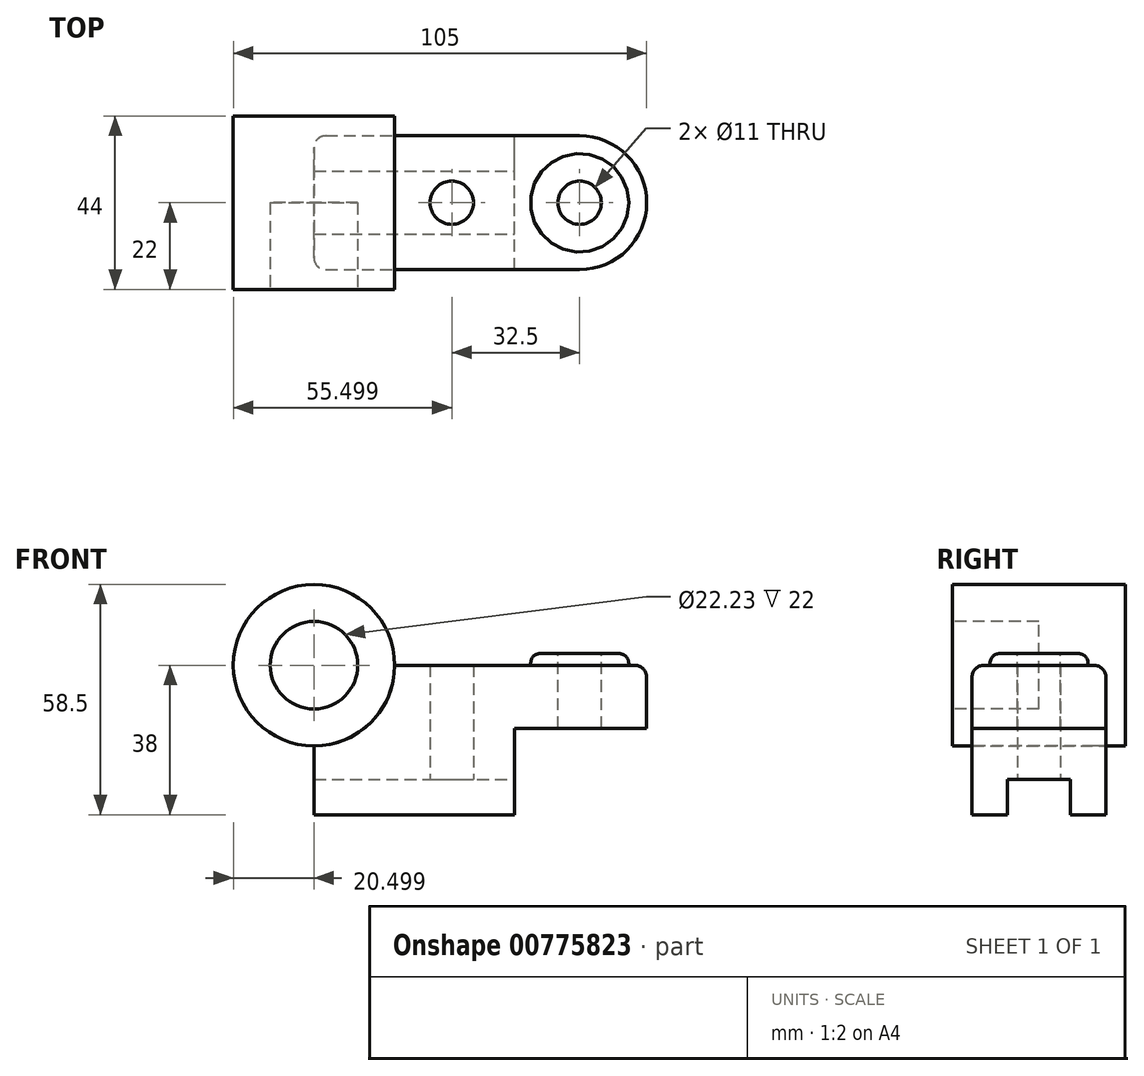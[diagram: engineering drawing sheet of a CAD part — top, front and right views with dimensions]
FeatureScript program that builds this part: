
annotation { "Feature Type Name" : "Feature", "Feature Type Description" : "" }
export const myFeature = defineFeature(function(context is Context, id is Id, definition is map)
    precondition{}
    {
        {
            var Q0;
            Q0=qCreatedBy(makeId("Front.planeOp"),FACE);
            var sketch = newSketch(context, id + "F0", { "sketchPlane" : qUnion([Q0])});
            skLineSegment(sketch, "E0.bottom", {"start": v(-36.23, 1.48) * mm, "end": v(48.27, 1.48) * mm});
            skLineSegment(sketch, "E0.top", {"start": v(-36.23, -36.52) * mm, "end": v(48.27, -36.52) * mm});
            skLineSegment(sketch, "E0.left", {"start": v(-36.23, 1.48) * mm, "end": v(-36.23, -36.52) * mm});
            skLineSegment(sketch, "E0.right", {"start": v(48.27, 1.48) * mm, "end": v(48.27, -36.52) * mm});
            skLineSegment(sketch, "E1", {"start": v(48.27, -36.52) * mm, "end": v(14.77, -36.52) * mm});
            skLineSegment(sketch, "E2", {"start": v(14.77, -36.52) * mm, "end": v(14.77, -14.52) * mm});
            skLineSegment(sketch, "E3", {"start": v(14.77, -14.52) * mm, "end": v(48.27, -14.52) * mm});
            skLineSegment(sketch, "E4", {"start": v(48.27, -14.52) * mm, "end": v(48.27, -36.52) * mm});
            skSolve(sketch);
        }
        {
            var Q0;
            Q0=makeQuery(id+"F0.imprint","IMPRINT",FACE,{"disambiguationData":[TD([[makeQuery(id+"F0.imprint","IMPRINT",EDGE,{"derivedFrom":sQuery(id+"F0.wireOp",EDGE,"E0.bottom")}),-1.0]])]});
            extrude(context, id + "F1", {"entities" : qUnion([Q0]), "depth" : 34 * mm, "offsetDistance" : 25 * mm});
        }
        {
            var Q0;
            Q0=makeQuery(id+"F1.opExtrude","SWEPT_FACE",FACE,{"disambiguationData":[OSD([sQuery(id+"F0.wireOp",EDGE,"E2")])]});
            var sketch = newSketch(context, id + "F2", { "sketchPlane" : qUnion([Q0])});
            skLineSegment(sketch, "E5", {"start": v(-34, -36.52) * mm, "end": v(-25, -36.52) * mm});
            skLineSegment(sketch, "E6", {"start": v(-25, -36.52) * mm, "end": v(-25, -27.52) * mm});
            skLineSegment(sketch, "E7", {"start": v(-25, -27.52) * mm, "end": v(-9, -27.52) * mm});
            skLineSegment(sketch, "E8", {"start": v(-9, -27.52) * mm, "end": v(-9, -36.52) * mm});
            skLineSegment(sketch, "E9", {"start": v(-9, -36.52) * mm, "end": v(-25, -36.52) * mm});
            skSolve(sketch);
        }
        {
            var Q0;
            Q0=makeQuery(id+"F2.imprint","IMPRINT",FACE,{"disambiguationData":[TD([[makeQuery(id+"F2.imprint","IMPRINT",EDGE,{"derivedFrom":sQuery(id+"F2.wireOp",EDGE,"E6")}),-1.0]])]});
            extrude(context, id + "F3", {"entities" : qUnion([Q0]), "operationType" : NewBodyOperationType.REMOVE, "oppositeDirection" : true, "depth" : 100 * mm, "offsetDistance" : 25 * mm});
        }
        {
            var Q0;
            Q0=makeQuery(id+"F1.opExtrude","CAP_EDGE",EDGE,{"disambiguationData":[OSD([sQuery(id+"F0.wireOp",EDGE,"E0.right")])],"isStart":false});
            fillet(context, id + "F4", {"entities" : qUnion([Q0]), "radius" : 17 * mm, "tangentPropagation" : true, "allowEdgeOverflow" : false});
        }
        {
            var Q0;
            Q0=makeQuery(id+"F1.opExtrude","CAP_EDGE",EDGE,{"disambiguationData":[OSD([sQuery(id+"F0.wireOp",EDGE,"E0.right")])],"isStart":true});
            fillet(context, id + "F5", {"entities" : qUnion([Q0]), "radius" : 17 * mm, "tangentPropagation" : true, "allowEdgeOverflow" : false});
        }
        {
            var Q0;
            Q0=makeQuery(id+"F1.opExtrude","SWEPT_FACE",FACE,{"disambiguationData":[OSD([sQuery(id+"F0.wireOp",EDGE,"E0.bottom")])]});
            var sketch = newSketch(context, id + "F6", { "sketchPlane" : qUnion([Q0])});
            skLineSegment(sketch, "E10", {"start": v(31.27, 0) * mm, "end": v(31.27, -17) * mm});
            skCircle(sketch, "E11", {"center": v(31.27, -17) * mm, "radius": 12.5 * mm});
            skCircle(sketch, "E12", {"center": v(31.27, -17) * mm, "radius": 5.5 * mm});
            skSolve(sketch);
        }
        {
            var Q0;
            Q0=makeQuery(id+"F6.imprint","IMPRINT",FACE,{"disambiguationData":[TD([[makeQuery(id+"F6.imprint","IMPRINT",EDGE,{"derivedFrom":sQuery(id+"F6.wireOp",EDGE,"E12")}),1.0]])]});
            extrude(context, id + "F7", {"entities" : qUnion([Q0]), "operationType" : NewBodyOperationType.REMOVE, "oppositeDirection" : true, "depth" : 25 * mm, "offsetDistance" : 25 * mm});
        }
        {
            var Q0;
            Q0=makeQuery(id+"F1.opExtrude","SWEPT_FACE",FACE,{"disambiguationData":[OSD([sQuery(id+"F0.wireOp",EDGE,"E0.bottom")])]});
            var sketch = newSketch(context, id + "F8", { "sketchPlane" : qUnion([Q0])});
            skLineSegment(sketch, "E13", {"start": v(31.27, 0) * mm, "end": v(31.27, -17) * mm});
            skCircle(sketch, "E14", {"center": v(31.27, -17) * mm, "radius": 12.5 * mm});
            skSolve(sketch);
        }
        {
            var Q0;
            Q0=makeQuery(id+"F8.imprint","IMPRINT",FACE,{"disambiguationData":[TD([[makeQuery(id+"F8.imprint","IMPRINT",EDGE,{"derivedFrom":sQuery(id+"F8.wireOp",EDGE,"E14")}),1.0]])]});
            extrude(context, id + "F9", {"entities" : qUnion([Q0]), "operationType" : NewBodyOperationType.ADD, "depth" : 3 * mm, "offsetDistance" : 25 * mm});
        }
        {
            var Q0;
            Q0=makeQuery(id+"F1.opExtrude","CAP_FACE",FACE,{"disambiguationData":[OSD([sQuery(id+"F0.wireOp",EDGE,"E0.bottom"),sQuery(id+"F0.wireOp",EDGE,"E0.top"),sQuery(id+"F0.wireOp",EDGE,"E0.left"),sQuery(id+"F0.wireOp",EDGE,"E0.right"),sQuery(id+"F0.wireOp",EDGE,"E2"),sQuery(id+"F0.wireOp",EDGE,"E3")])],"isStart":false});
            var sketch = newSketch(context, id + "F10", { "sketchPlane" : qUnion([Q0])});
            skCircle(sketch, "E15", {"center": v(-36.23, 1.48) * mm, "radius": 20.5 * mm});
            skCircle(sketch, "E16", {"center": v(-36.23, 1.48) * mm, "radius": 11.12 * mm});
            skSolve(sketch);
        }
        {
            var Q0;
            {var subQ0=sQuery(id+"F10.wireOp",EDGE,"E16");var subQ1=makeQuery(id+"F1.opExtrude","CAP_EDGE",EDGE,{"disambiguationData":[OSD([sQuery(id+"F0.wireOp",EDGE,"E0.left")])],"isStart":false});var subQ2=makeQuery(id+"F10.imprint","INTERSECT",VERTEX,{"derivedFrom":[subQ1,subQ0]});Q0=makeQuery(id+"F10.imprint","IMPRINT",FACE,{"disambiguationData":[TD([[makeQuery(id+"F10.imprint","IMPRINT",EDGE,{"disambiguationData":[TD([[subQ2,-1.0]])],"derivedFrom":subQ0}),1.0]])]});}
            var Q1;
            {var subQ0=sQuery(id+"F10.wireOp",EDGE,"E15");var subQ1=makeQuery(id+"F1.opExtrude","CAP_EDGE",EDGE,{"disambiguationData":[OSD([sQuery(id+"F0.wireOp",EDGE,"E0.left")])],"isStart":false});var subQ2=makeQuery(id+"F10.imprint","INTERSECT",VERTEX,{"derivedFrom":[subQ1,subQ0]});Q1=makeQuery(id+"F10.imprint","IMPRINT",FACE,{"disambiguationData":[TD([[makeQuery(id+"F10.imprint","IMPRINT",EDGE,{"disambiguationData":[TD([[subQ2,-1.0]])],"derivedFrom":subQ0}),1.0]])]});}
            extrude(context, id + "F11", {"entities" : qUnion([Q0, Q1]), "operationType" : NewBodyOperationType.REMOVE, "oppositeDirection" : true, "depth" : 50 * mm, "offsetDistance" : 25 * mm});
        }
        {
            var Q0;
            Q0=qCreatedBy(makeId("Front.planeOp"),FACE);
            var sketch = newSketch(context, id + "F12", { "sketchPlane" : qUnion([Q0])});
            skCircle(sketch, "E17", {"center": v(-36.23, 1.48) * mm, "radius": 20.5 * mm});
            skCircle(sketch, "E18", {"center": v(-36.23, 1.48) * mm, "radius": 11.12 * mm});
            skSolve(sketch);
        }
        {
            var Q0;
            Q0=makeQuery(id+"F12.imprint","IMPRINT",FACE,{"disambiguationData":[TD([[makeQuery(id+"F12.imprint","IMPRINT",EDGE,{"derivedFrom":sQuery(id+"F12.wireOp",EDGE,"E18")}),1.0]])]});
            var Q1;
            Q1=makeQuery(id+"F12.imprint","IMPRINT",FACE,{"disambiguationData":[TD([[makeQuery(id+"F12.imprint","IMPRINT",EDGE,{"derivedFrom":sQuery(id+"F12.wireOp",EDGE,"E17")}),1.0]])]});
            extrude(context, id + "F13", {"entities" : qUnion([Q0, Q1]), "depth" : 5 * mm, "offsetDistance" : 25 * mm});
        }
        {
            var Q0;
            Q0=makeQuery(id+"F13.opExtrude","CAP_FACE",FACE,{"disambiguationData":[OSD([sQuery(id+"F12.wireOp",EDGE,"E17")])],"isStart":false});
            var sketch = newSketch(context, id + "F14", { "sketchPlane" : qUnion([Q0])});
            skCircle(sketch, "E19", {"center": v(-36.23, 1.48) * mm, "radius": 20.5 * mm});
            skSolve(sketch);
        }
        {
            var Q0;
            Q0 = qSketchRegion(id + "F14", true);
            extrude(context, id + "F15", {"entities" : qUnion([Q0]), "operationType" : NewBodyOperationType.ADD, "depth" : 39 * mm, "offsetDistance" : 25 * mm});
        }
        {
            var Q0;
            Q0=makeQuery(id+"F13.opExtrude","CAP_FACE",FACE,{"disambiguationData":[OSD([sQuery(id+"F12.wireOp",EDGE,"E17")])],"isStart":true});
            var sketch = newSketch(context, id + "F16", { "sketchPlane" : qUnion([Q0])});
            skCircle(sketch, "E20", {"center": v(36.23, 1.48) * mm, "radius": 20.5 * mm});
            skSolve(sketch);
        }
        {
            var Q0;
            Q0 = qSketchRegion(id + "F16", true);
            extrude(context, id + "F17", {"entities" : qUnion([Q0]), "operationType" : NewBodyOperationType.ADD, "depth" : 5 * mm, "offsetDistance" : 25 * mm});
        }
        {
            var Q0;
            Q0=makeQuery(id+"F15.opExtrude","CAP_FACE",FACE,{"disambiguationData":[OSD([sQuery(id+"F14.wireOp",EDGE,"E19")])],"isStart":false});
            var sketch = newSketch(context, id + "F18", { "sketchPlane" : qUnion([Q0])});
            skCircle(sketch, "E21", {"center": v(-36.23, 1.48) * mm, "radius": 20.5 * mm});
            skSolve(sketch);
        }
        {
            var Q0;
            Q0 = qSketchRegion(id + "F18", true);
            extrude(context, id + "F19", {"entities" : qUnion([Q0]), "operationType" : NewBodyOperationType.REMOVE, "oppositeDirection" : true, "depth" : 5 * mm, "offsetDistance" : 25 * mm});
        }
        {
            var Q0;
            Q0=makeQuery(id+"F19.boolean.opBoolean","COPY",FACE,{"derivedFrom":makeQuery(id+"F19.opExtrude","CAP_FACE",FACE,{"disambiguationData":[OSD([sQuery(id+"F18.wireOp",EDGE,"E21")])],"isStart":false})});
            var sketch = newSketch(context, id + "F20", { "sketchPlane" : qUnion([Q0])});
            skCircle(sketch, "E22", {"center": v(-36.23, 1.48) * mm, "radius": 11.12 * mm});
            skSolve(sketch);
        }
        {
            var Q0;
            Q0=makeQuery(id+"F20.imprint","IMPRINT",FACE,{"disambiguationData":[TD([[makeQuery(id+"F20.imprint","IMPRINT",EDGE,{"derivedFrom":sQuery(id+"F20.wireOp",EDGE,"E22")}),1.0]])]});
            extrude(context, id + "F21", {"entities" : qUnion([Q0]), "operationType" : NewBodyOperationType.REMOVE, "oppositeDirection" : true, "depth" : 22 * mm, "offsetDistance" : 25 * mm});
        }
        {
            var Q0;
            Q0=makeQuery(id+"F3.boolean.opBoolean","COPY",FACE,{"derivedFrom":makeQuery(id+"F3.opExtrude","SWEPT_FACE",FACE,{"disambiguationData":[OSD([sQuery(id+"F2.wireOp",EDGE,"E7")])]})});
            var sketch = newSketch(context, id + "F22", { "sketchPlane" : qUnion([Q0])});
            skLineSegment(sketch, "E23", {"start": v(-36.23, 9) * mm, "end": v(-36.23, 17) * mm});
            skLineSegment(sketch, "E24", {"start": v(-36.23, 17) * mm, "end": v(-1.23, 17) * mm});
            skCircle(sketch, "E25", {"center": v(-1.23, 17) * mm, "radius": 5.5 * mm});
            skSolve(sketch);
        }
        {
            var Q0;
            Q0=makeQuery(id+"F22.imprint","IMPRINT",FACE,{"disambiguationData":[TD([[makeQuery(id+"F22.imprint","IMPRINT",EDGE,{"derivedFrom":sQuery(id+"F22.wireOp",EDGE,"E25")}),1.0]])]});
            extrude(context, id + "F23", {"entities" : qUnion([Q0]), "operationType" : NewBodyOperationType.REMOVE, "oppositeDirection" : true, "depth" : 25 * mm, "offsetDistance" : 25 * mm});
        }
        {
            var Q0;
            Q0=makeQuery(id+"F23.boolean.opBoolean","COPY",FACE,{"derivedFrom":makeQuery(id+"F23.opExtrude","CAP_FACE",FACE,{"disambiguationData":[OSD([sQuery(id+"F22.wireOp",EDGE,"E25")])],"isStart":false})});
            extrude(context, id + "F24", {"entities" : qUnion([Q0]), "operationType" : NewBodyOperationType.REMOVE, "oppositeDirection" : true, "depth" : 25 * mm, "offsetDistance" : 25 * mm});
        }
        {
            var Q0;
            Q0=makeQuery(id+"F1.opExtrude","CAP_EDGE",EDGE,{"disambiguationData":[OSD([sQuery(id+"F0.wireOp",EDGE,"E0.bottom")])],"isStart":true});
            var Q1;
            Q1=makeQuery(id+"F5.opFillet","BLEND_EDGE",EDGE,{"blendedFrom":[makeQuery(id+"F1.opExtrude","CAP_EDGE",EDGE,{"disambiguationData":[OSD([sQuery(id+"F0.wireOp",EDGE,"E0.right")])],"isStart":true}),makeQuery(id+"F1.opExtrude","SWEPT_FACE",FACE,{"disambiguationData":[OSD([sQuery(id+"F0.wireOp",EDGE,"E0.bottom")])]})],"blendedInto":[makeQuery(id+"F1.opExtrude","SWEPT_FACE",FACE,{"disambiguationData":[OSD([sQuery(id+"F0.wireOp",EDGE,"E0.bottom")])]})]});
            var Q2;
            Q2=makeQuery(id+"F4.opFillet","BLEND_EDGE",EDGE,{"blendedFrom":[makeQuery(id+"F1.opExtrude","CAP_EDGE",EDGE,{"disambiguationData":[OSD([sQuery(id+"F0.wireOp",EDGE,"E0.right")])],"isStart":false}),makeQuery(id+"F1.opExtrude","SWEPT_FACE",FACE,{"disambiguationData":[OSD([sQuery(id+"F0.wireOp",EDGE,"E0.bottom")])]})],"blendedInto":[makeQuery(id+"F1.opExtrude","SWEPT_FACE",FACE,{"disambiguationData":[OSD([sQuery(id+"F0.wireOp",EDGE,"E0.bottom")])]})]});
            var Q3;
            Q3=makeQuery(id+"F1.opExtrude","CAP_EDGE",EDGE,{"disambiguationData":[OSD([sQuery(id+"F0.wireOp",EDGE,"E0.bottom")])],"isStart":false});
            var Q4;
            Q4=makeQuery(id+"F11.boolean.opBoolean","COPY",EDGE,{"derivedFrom":makeQuery(id+"F11.opExtrude","SWEPT_EDGE",EDGE,{"disambiguationData":[OSD([sQuery(id+"F0.wireOp",EDGE,"E0.bottom"),sQuery(id+"F10.wireOp",EDGE,"E15")])]})});
            fillet(context, id + "F25", {"entities" : qUnion([Q0, Q1, Q2, Q3, Q4]), "radius" : 3.1 * mm, "tangentPropagation" : true, "allowEdgeOverflow" : false});
        }
        {
            var Q0;
            Q0=makeQuery(id+"F1.opExtrude","CAP_EDGE",EDGE,{"disambiguationData":[OSD([sQuery(id+"F0.wireOp",EDGE,"E0.left")])],"isStart":true});
            var Q1;
            Q1=makeQuery(id+"F1.opExtrude","CAP_EDGE",EDGE,{"disambiguationData":[OSD([sQuery(id+"F0.wireOp",EDGE,"E0.left")])],"isStart":false});
            fillet(context, id + "F26", {"entities" : qUnion([Q0, Q1]), "radius" : 3 * mm, "tangentPropagation" : true, "allowEdgeOverflow" : false});
        }
        {
            var Q0;
            Q0=makeQuery(id+"F9.opExtrude","CAP_EDGE",EDGE,{"disambiguationData":[OSD([sQuery(id+"F8.wireOp",EDGE,"E14")])],"isStart":false});
            fillet(context, id + "F27", {"entities" : qUnion([Q0]), "radius" : 3 * mm, "rho" : 0.5, "crossSection" : FilletCrossSection.CONIC, "allowEdgeOverflow" : false});
        }
    });
